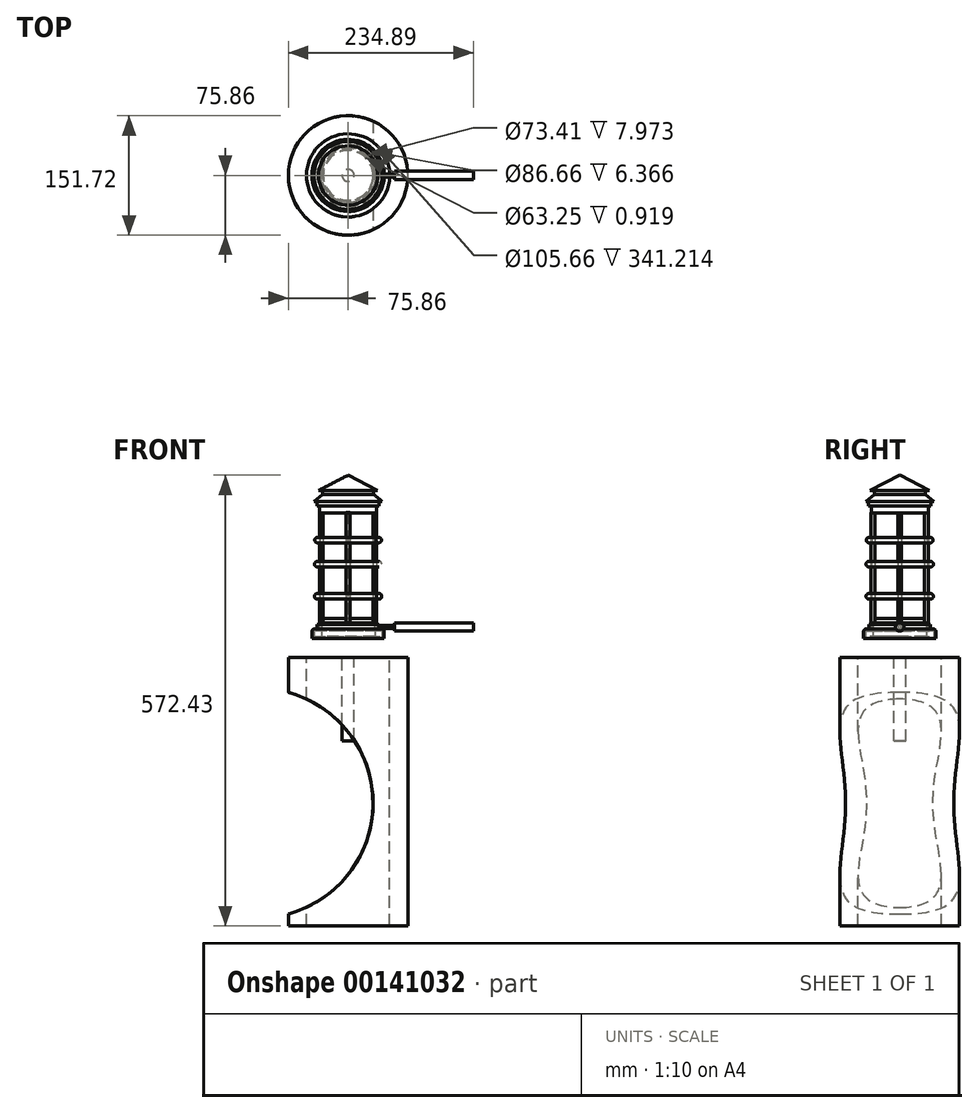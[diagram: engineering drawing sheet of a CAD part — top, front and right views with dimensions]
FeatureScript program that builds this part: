
annotation { "Feature Type Name" : "Feature", "Feature Type Description" : "" }
export const myFeature = defineFeature(function(context is Context, id is Id, definition is map)
    precondition{}
    {
        {
            var Q0;
            Q0=qCreatedBy(makeId("Front.planeOp"),FACE);
            var sketch = newSketch(context, id + "F0", { "sketchPlane" : qUnion([Q0])});
            skLineSegment(sketch, "E0", {"start": v(0, -64.78) * mm, "end": v(-52.83, -64.78) * mm});
            skLineSegment(sketch, "E1", {"start": v(-52.83, -64.78) * mm, "end": v(-45.18, -57.68) * mm});
            skLineSegment(sketch, "E2", {"start": v(-45.18, -57.68) * mm, "end": v(-45.18, -42.8) * mm});
            skLineSegment(sketch, "E3", {"start": v(-45.18, -42.8) * mm, "end": v(-47.57, -42.8) * mm});
            skLineSegment(sketch, "E4", {"start": v(-47.57, -42.8) * mm, "end": v(-47.57, -40.94) * mm});
            skLineSegment(sketch, "E5", {"start": v(-47.57, -40.94) * mm, "end": v(0, -40.94) * mm});
            skLineSegment(sketch, "E6", {"start": v(0, -40.94) * mm, "end": v(0, -64.78) * mm, "construction": true});
            skSolve(sketch);
        }
        {
            var Q0;
            Q0=sQuery(id+"F0.wireOp",EDGE,"E5");
            var Q1;
            Q1=sQuery(id+"F0.wireOp",EDGE,"E4");
            var Q2;
            Q2=sQuery(id+"F0.wireOp",EDGE,"E3");
            var Q3;
            Q3=sQuery(id+"F0.wireOp",EDGE,"E2");
            var Q4;
            Q4=sQuery(id+"F0.wireOp",EDGE,"E1");
            var Q5;
            Q5=sQuery(id+"F0.wireOp",EDGE,"E0");
            var Q6;
            Q6=sQuery(id+"F0.wireOp",EDGE,"E6");
            revolve(context, id + "F1", {"bodyType" : ToolBodyType.SURFACE, "surfaceEntities" : qUnion([Q0, Q1, Q2, Q3, Q4, Q5]), "axis" : qUnion([Q6]), "revolveType" : RevolveType.FULL});
        }
        {
            var Q0;
            Q0=makeQuery(id+"F1.opRevolve","SWEPT_FACE",FACE,{"disambiguationData":[OSD([sQuery(id+"F0.wireOp",EDGE,"E5")])]});
            var sketch = newSketch(context, id + "F2", { "sketchPlane" : qUnion([Q0])});
            skCircle(sketch, "E7", {"center": v(0, 0) * mm, "radius": 45.87 * mm});
            skSolve(sketch);
        }
        {
            var Q0;
            Q0=makeQuery(id+"F2.imprint","IMPRINT",FACE,{"disambiguationData":[TD([[makeQuery(id+"F2.imprint","IMPRINT",EDGE,{"derivedFrom":sQuery(id+"F2.wireOp",EDGE,"E7")}),1.0]])]});
            extrude(context, id + "F3", {"entities" : qUnion([Q0]), "depth" : 12.23 * mm});
        }
        {
            var Q0;
            Q0=makeQuery(id+"F3.opExtrude","CAP_EDGE",EDGE,{"disambiguationData":[OSD([sQuery(id+"F2.wireOp",EDGE,"E7")])],"isStart":false});
            fillet(context, id + "F4", {"entities" : qUnion([Q0]), "radius" : 3.32 * mm, "tangentPropagation" : true, "allowEdgeOverflow" : false});
        }
        {
            var Q0;
            Q0=makeQuery(id+"F3.opExtrude","CAP_FACE",FACE,{"disambiguationData":[OSD([sQuery(id+"F2.wireOp",EDGE,"E7")])],"isStart":false});
            var sketch = newSketch(context, id + "F5", { "sketchPlane" : qUnion([Q0])});
            skCircle(sketch, "E8", {"center": v(0, 0) * mm, "radius": 39.24 * mm});
            skSolve(sketch);
        }
        {
            var Q0;
            Q0=makeQuery(id+"F5.imprint","IMPRINT",FACE,{"disambiguationData":[TD([[makeQuery(id+"F5.imprint","IMPRINT",EDGE,{"derivedFrom":sQuery(id+"F5.wireOp",EDGE,"E8")}),1.0]])]});
            extrude(context, id + "F6", {"entities" : qUnion([Q0]), "operationType" : NewBodyOperationType.ADD, "depth" : 5.43 * mm});
        }
        {
            var Q0;
            Q0=makeQuery(id+"F6.opExtrude","CAP_FACE",FACE,{"disambiguationData":[OSD([sQuery(id+"F5.wireOp",EDGE,"E8")])],"isStart":false});
            shell(context, id + "F7", {"entities" : qUnion([Q0]), "thickness" : 2.54 * mm});
        }
        {
            var Q0;
            {var subQ0=sQuery(id+"F2.wireOp",EDGE,"E7");Q0=makeQuery(id+"F7.opShell","OFFSET_FACE",FACE,{"disambiguationData":[OSD([subQ0]),TDD([makeQuery(id+"F3.opExtrude","CAP_FACE",FACE,{"disambiguationData":[OSD([subQ0])],"isStart":true})])]});}
            var sketch = newSketch(context, id + "F8", { "sketchPlane" : qUnion([Q0])});
            skCircle(sketch, "E9", {"center": v(0, 0) * mm, "radius": 33.95 * mm});
            skSolve(sketch);
        }
        {
            var Q0;
            Q0=qSketchRegion(id+"F8",true);
            extrude(context, id + "F9", {"entities" : qUnion([Q0]), "operationType" : NewBodyOperationType.ADD, "depth" : 17.16 * mm});
        }
        {
            var Q0;
            Q0=makeQuery(id+"F9.opExtrude","CAP_FACE",FACE,{"disambiguationData":[OSD([sQuery(id+"F8.wireOp",EDGE,"E9")])],"isStart":false});
            var sketch = newSketch(context, id + "F10", { "sketchPlane" : qUnion([Q0])});
            skCircle(sketch, "E10", {"center": v(0, 0) * mm, "radius": 31.65 * mm});
            skSolve(sketch);
        }
        {
            var Q0;
            Q0=qSketchRegion(id+"F10",true);
            extrude(context, id + "F11", {"entities" : qUnion([Q0]), "operationType" : NewBodyOperationType.ADD, "depth" : 5.86 * mm});
        }
        {
            var Q0;
            Q0=makeQuery(id+"F9.opExtrude","CAP_FACE",FACE,{"disambiguationData":[OSD([sQuery(id+"F8.wireOp",EDGE,"E9")])],"isStart":false});
            var sketch = newSketch(context, id + "F12", { "sketchPlane" : qUnion([Q0])});
            skCircle(sketch, "E11", {"center": v(33.95, 0) * mm, "radius": 2.3 * mm});
            skCircle(sketch, "E12", {"center": v(-33.95, 0) * mm, "radius": 2.3 * mm});
            skCircle(sketch, "E13", {"center": v(0, 33.95) * mm, "radius": 2.3 * mm});
            skCircle(sketch, "E14", {"center": v(0, -33.95) * mm, "radius": 2.34 * mm});
            skSolve(sketch);
        }
        {
            var Q0;
            {var subQ0=sQuery(id+"F12.wireOp",EDGE,"E11");var subQ1=makeQuery(id+"F9.opExtrude","CAP_EDGE",EDGE,{"disambiguationData":[OSD([sQuery(id+"F8.wireOp",EDGE,"E9")])],"isStart":false});var subQ2=makeQuery(id+"F12.imprint","INTERSECT",VERTEX,{"disambiguationData":[OD(0.0)],"derivedFrom":[subQ1,subQ0]});Q0=makeQuery(id+"F12.imprint","IMPRINT",FACE,{"disambiguationData":[TD([[makeQuery(id+"F12.imprint","IMPRINT",EDGE,{"disambiguationData":[TD([[subQ2,1.0]])],"derivedFrom":subQ0}),1.0]])]});}
            var Q1;
            {var subQ0=sQuery(id+"F12.wireOp",EDGE,"E12");var subQ1=makeQuery(id+"F9.opExtrude","CAP_EDGE",EDGE,{"disambiguationData":[OSD([sQuery(id+"F8.wireOp",EDGE,"E9")])],"isStart":false});var subQ2=makeQuery(id+"F12.imprint","INTERSECT",VERTEX,{"disambiguationData":[OD(0.0)],"derivedFrom":[subQ1,subQ0]});Q1=makeQuery(id+"F12.imprint","IMPRINT",FACE,{"disambiguationData":[TD([[makeQuery(id+"F12.imprint","IMPRINT",EDGE,{"disambiguationData":[TD([[subQ2,1.0]])],"derivedFrom":subQ0}),1.0]])]});}
            var Q2;
            {var subQ0=sQuery(id+"F12.wireOp",EDGE,"E13");var subQ1=makeQuery(id+"F9.opExtrude","CAP_EDGE",EDGE,{"disambiguationData":[OSD([sQuery(id+"F8.wireOp",EDGE,"E9")])],"isStart":false});var subQ2=makeQuery(id+"F12.imprint","INTERSECT",VERTEX,{"disambiguationData":[OD(0.0)],"derivedFrom":[subQ1,subQ0]});Q2=makeQuery(id+"F12.imprint","IMPRINT",FACE,{"disambiguationData":[TD([[makeQuery(id+"F12.imprint","IMPRINT",EDGE,{"disambiguationData":[TD([[subQ2,1.0]])],"derivedFrom":subQ0}),1.0]])]});}
            var Q3;
            {var subQ0=sQuery(id+"F12.wireOp",EDGE,"E13");var subQ1=makeQuery(id+"F9.opExtrude","CAP_EDGE",EDGE,{"disambiguationData":[OSD([sQuery(id+"F8.wireOp",EDGE,"E9")])],"isStart":false});var subQ2=makeQuery(id+"F12.imprint","INTERSECT",VERTEX,{"disambiguationData":[OD(0.0)],"derivedFrom":[subQ1,subQ0]});Q3=makeQuery(id+"F12.imprint","IMPRINT",FACE,{"disambiguationData":[TD([[makeQuery(id+"F12.imprint","IMPRINT",EDGE,{"disambiguationData":[TD([[subQ2,-1.0]])],"derivedFrom":subQ0}),1.0]])]});}
            var Q4;
            {var subQ0=sQuery(id+"F12.wireOp",EDGE,"E12");var subQ1=makeQuery(id+"F9.opExtrude","CAP_EDGE",EDGE,{"disambiguationData":[OSD([sQuery(id+"F8.wireOp",EDGE,"E9")])],"isStart":false});var subQ2=makeQuery(id+"F12.imprint","INTERSECT",VERTEX,{"disambiguationData":[OD(0.0)],"derivedFrom":[subQ1,subQ0]});Q4=makeQuery(id+"F12.imprint","IMPRINT",FACE,{"disambiguationData":[TD([[makeQuery(id+"F12.imprint","IMPRINT",EDGE,{"disambiguationData":[TD([[subQ2,-1.0]])],"derivedFrom":subQ0}),1.0]])]});}
            var Q5;
            {var subQ0=sQuery(id+"F12.wireOp",EDGE,"E11");var subQ1=makeQuery(id+"F9.opExtrude","CAP_EDGE",EDGE,{"disambiguationData":[OSD([sQuery(id+"F8.wireOp",EDGE,"E9")])],"isStart":false});var subQ2=makeQuery(id+"F12.imprint","INTERSECT",VERTEX,{"disambiguationData":[OD(0.0)],"derivedFrom":[subQ1,subQ0]});Q5=makeQuery(id+"F12.imprint","IMPRINT",FACE,{"disambiguationData":[TD([[makeQuery(id+"F12.imprint","IMPRINT",EDGE,{"disambiguationData":[TD([[subQ2,-1.0]])],"derivedFrom":subQ0}),1.0]])]});}
            var Q6;
            {var subQ0=sQuery(id+"F12.wireOp",EDGE,"E14");var subQ1=makeQuery(id+"F9.opExtrude","CAP_EDGE",EDGE,{"disambiguationData":[OSD([sQuery(id+"F8.wireOp",EDGE,"E9")])],"isStart":false});var subQ2=makeQuery(id+"F12.imprint","INTERSECT",VERTEX,{"disambiguationData":[OD(0.0)],"derivedFrom":[subQ1,subQ0]});Q6=makeQuery(id+"F12.imprint","IMPRINT",FACE,{"disambiguationData":[TD([[makeQuery(id+"F12.imprint","IMPRINT",EDGE,{"disambiguationData":[TD([[subQ2,-1.0]])],"derivedFrom":subQ0}),1.0]])]});}
            var Q7;
            {var subQ0=sQuery(id+"F12.wireOp",EDGE,"E14");var subQ1=makeQuery(id+"F9.opExtrude","CAP_EDGE",EDGE,{"disambiguationData":[OSD([sQuery(id+"F8.wireOp",EDGE,"E9")])],"isStart":false});var subQ2=makeQuery(id+"F12.imprint","INTERSECT",VERTEX,{"disambiguationData":[OD(0.0)],"derivedFrom":[subQ1,subQ0]});Q7=makeQuery(id+"F12.imprint","IMPRINT",FACE,{"disambiguationData":[TD([[makeQuery(id+"F12.imprint","IMPRINT",EDGE,{"disambiguationData":[TD([[subQ2,1.0]])],"derivedFrom":subQ0}),1.0]])]});}
            extrude(context, id + "F13", {"entities" : qUnion([Q0, Q1, Q2, Q3, Q4, Q5, Q6, Q7]), "depth" : 140.45 * mm});
        }
        {
            var Q0;
            Q0=makeQuery(id+"F11.opExtrude","CAP_FACE",FACE,{"disambiguationData":[OSD([sQuery(id+"F10.wireOp",EDGE,"E10")])],"isStart":false});
            extrude(context, id + "F14", {"entities" : qUnion([Q0]), "depth" : 134.56 * mm});
        }
        {
            var Q0;
            Q0=makeQuery(id+"F14.opExtrude","CAP_FACE",FACE,{"disambiguationData":[OSD([sQuery(id+"F10.wireOp",EDGE,"E10")])],"isStart":false});
            shell(context, id + "F15", {"entities" : qUnion([Q0]), "thickness" : 0.03 * mm});
        }
        {
            var Q0;
            {var subQ0=sQuery(id+"F10.wireOp",EDGE,"E10");Q0=makeQuery(id+"F15.opShell","OFFSET_FACE",FACE,{"disambiguationData":[OSD([subQ0]),TDD([makeQuery(id+"F14.opExtrude","CAP_FACE",FACE,{"disambiguationData":[OSD([subQ0])],"isStart":true})])]});}
            extrude(context, id + "F16", {"entities" : qUnion([Q0]), "operationType" : NewBodyOperationType.ADD, "depth" : 133.61 * mm});
        }
        {
            var Q0;
            Q0=makeQuery(id+"F16.opExtrude","CAP_FACE",FACE,{"disambiguationData":[OSD([sQuery(id+"F10.wireOp",EDGE,"E10")])],"isStart":false});
            var sketch = newSketch(context, id + "F17", { "sketchPlane" : qUnion([Q0])});
            skCircle(sketch, "E15", {"center": v(0, 0) * mm, "radius": 36.18 * mm});
            skSolve(sketch);
        }
        {
            var Q0;
            Q0=qSketchRegion(id+"F17",true);
            extrude(context, id + "F18", {"entities" : qUnion([Q0]), "depth" : 8.96 * mm});
        }
        {
            var Q0;
            Q0=makeQuery(id+"F18.opExtrude","CAP_FACE",FACE,{"disambiguationData":[OSD([sQuery(id+"F17.wireOp",EDGE,"E15")])],"isStart":false});
            var sketch = newSketch(context, id + "F19", { "sketchPlane" : qUnion([Q0])});
            skCircle(sketch, "E16", {"center": v(0, 0) * mm, "radius": 39.6 * mm});
            skSolve(sketch);
        }
        {
            var Q0;
            Q0=makeQuery(id+"F19.imprint","IMPRINT",FACE,{"disambiguationData":[TD([[makeQuery(id+"F19.imprint","IMPRINT",EDGE,{"derivedFrom":sQuery(id+"F19.wireOp",EDGE,"E16")}),1.0]])]});
            var Q1;
            Q1=makeQuery(id+"F19.imprint","IMPRINT",FACE,{"disambiguationData":[TD([[makeQuery(id+"F19.imprint","IMPRINT",EDGE,{"derivedFrom":makeQuery(id+"F18.opExtrude","CAP_EDGE",EDGE,{"disambiguationData":[OSD([sQuery(id+"F17.wireOp",EDGE,"E15")])],"isStart":false})}),1.0]])]});
            extrude(context, id + "F20", {"entities" : qUnion([Q0, Q1]), "operationType" : NewBodyOperationType.ADD, "depth" : 6.14 * mm});
        }
        {
            var Q0;
            Q0=makeQuery(id+"F20.opExtrude","CAP_FACE",FACE,{"disambiguationData":[OSD([sQuery(id+"F19.wireOp",EDGE,"E16")])],"isStart":false});
            var sketch = newSketch(context, id + "F21", { "sketchPlane" : qUnion([Q0])});
            skSolve(sketch);
        }
        {
            var Q0;
            Q0=makeQuery(id+"F21.imprint","IMPRINT",FACE,{"disambiguationData":[TD([[makeQuery(id+"F21.imprint","IMPRINT",EDGE,{"derivedFrom":makeQuery(id+"F20.opExtrude","CAP_EDGE",EDGE,{"disambiguationData":[OSD([sQuery(id+"F19.wireOp",EDGE,"E16")])],"isStart":false})}),1.0]])]});
            var sketch = newSketch(context, id + "F22", { "sketchPlane" : qUnion([Q0])});
            skSolve(sketch);
        }
        {
            var Q0;
            Q0=makeQuery(id+"F22.imprint","IMPRINT",FACE,{"disambiguationData":[TD([[makeQuery(id+"F22.imprint","IMPRINT",EDGE,{"derivedFrom":makeQuery(id+"F21.imprint","IMPRINT",EDGE,{"derivedFrom":makeQuery(id+"F20.opExtrude","CAP_EDGE",EDGE,{"disambiguationData":[OSD([sQuery(id+"F19.wireOp",EDGE,"E16")])],"isStart":false})})}),1.0]])]});
            var sketch = newSketch(context, id + "F23", { "sketchPlane" : qUnion([Q0])});
            skCircle(sketch, "E17", {"center": v(0, 0) * mm, "radius": 5.35 * mm});
            skSolve(sketch);
        }
        {
            var Q0;
            Q0=makeQuery(id+"F23.imprint","IMPRINT",FACE,{"disambiguationData":[TD([[makeQuery(id+"F23.imprint","IMPRINT",EDGE,{"derivedFrom":sQuery(id+"F23.wireOp",EDGE,"E17")}),1.0]])]});
            extrude(context, id + "F24", {"entities" : qUnion([Q0]), "operationType" : NewBodyOperationType.ADD, "depth" : 28.78 * mm});
        }
        {
            var Q0;
            Q0=qCreatedBy(makeId("Front.planeOp"),FACE);
            var sketch = newSketch(context, id + "F25", { "sketchPlane" : qUnion([Q0])});
            skLineSegment(sketch, "E18", {"start": v(0, 148) * mm, "end": v(0, 133.15) * mm});
            skLineSegment(sketch, "E19", {"start": v(0, 133.15) * mm, "end": v(43.2, 133.15) * mm});
            skLineSegment(sketch, "E20", {"start": v(43.2, 133.15) * mm, "end": v(32.35, 142.24) * mm});
            skLineSegment(sketch, "E21", {"start": v(32.35, 142.24) * mm, "end": v(32.35, 147.08) * mm});
            skLineSegment(sketch, "E22", {"start": v(32.35, 147.08) * mm, "end": v(37.62, 147.08) * mm});
            skLineSegment(sketch, "E23", {"start": v(37.62, 147.08) * mm, "end": v(0, 166.44) * mm});
            skLineSegment(sketch, "E24", {"start": v(0, 166.44) * mm, "end": v(0, 148) * mm});
            skSolve(sketch);
        }
        {
            var Q0;
            Q0=makeQuery(id+"F25.imprint","IMPRINT",FACE,{"disambiguationData":[TD([[makeQuery(id+"F25.imprint","IMPRINT",EDGE,{"derivedFrom":sQuery(id+"F25.wireOp",EDGE,"E18")}),1.0]])]});
            var Q1;
            Q1=sQuery(id+"F25.wireOp",EDGE,"E24");
            revolve(context, id + "F26", {"operationType" : NewBodyOperationType.ADD, "entities" : qUnion([Q0]), "axis" : qUnion([Q1]), "revolveType" : RevolveType.FULL});
        }
        {
            var Q0;
            Q0=qCreatedBy(makeId("Right.planeOp"),FACE);
            var sketch = newSketch(context, id + "F27", { "sketchPlane" : qUnion([Q0])});
            skCircle(sketch, "E25", {"center": v(-39.38, 53.45) * mm, "radius": 3.44 * mm});
            skCircle(sketch, "E26", {"center": v(-39.3, 12.6) * mm, "radius": 3.5 * mm});
            skCircle(sketch, "E27", {"center": v(-38.89, 84.08) * mm, "radius": 3.5 * mm});
            skSolve(sketch);
        }
        {
            var Q0;
            Q0=sQuery(id+"F27.wireOp",EDGE,"E25");
            var Q1;
            Q1=makeQuery(id+"F14.opExtrude","SWEPT_FACE",FACE,{"disambiguationData":[OSD([sQuery(id+"F10.wireOp",EDGE,"E10")])]});
            revolve(context, id + "F28", {"bodyType" : ToolBodyType.SURFACE, "surfaceEntities" : qUnion([Q0]), "axis" : qUnion([Q1]), "revolveType" : RevolveType.FULL});
        }
        {
            var Q0;
            Q0=qSketchRegion(id+"F27",true);
            var Q1;
            Q1=makeQuery(id+"F14.opExtrude","SWEPT_FACE",FACE,{"disambiguationData":[OSD([sQuery(id+"F10.wireOp",EDGE,"E10")])]});
            revolve(context, id + "F29", {"entities" : qUnion([Q0]), "axis" : qUnion([Q1]), "revolveType" : RevolveType.FULL});
        }
        {
            var Q0;
            Q0=qSketchRegion(id+"F27",true);
            var Q1;
            Q1=makeQuery(id+"F14.opExtrude","SWEPT_FACE",FACE,{"disambiguationData":[OSD([sQuery(id+"F10.wireOp",EDGE,"E10")])]});
            revolve(context, id + "F30", {"entities" : qUnion([Q0]), "axis" : qUnion([Q1]), "revolveType" : RevolveType.FULL});
        }
        {
            var Q0;
            Q0=qCreatedBy(makeId("Right.planeOp"),FACE);
            var sketch = newSketch(context, id + "F31", { "sketchPlane" : qUnion([Q0])});
            skCircle(sketch, "E28", {"center": v(0, -26.4) * mm, "radius": 1.99 * mm});
            skSolve(sketch);
        }
        {
            var Q0;
            Q0=qSketchRegion(id+"F31",true);
            extrude(context, id + "F32", {"entities" : qUnion([Q0]), "operationType" : NewBodyOperationType.ADD, "depth" : 64.6 * mm});
        }
        {
            var Q0;
            Q0=makeQuery(id+"F32.opExtrude","CAP_FACE",FACE,{"disambiguationData":[OSD([sQuery(id+"F31.wireOp",EDGE,"E28")])],"isStart":false});
            var sketch = newSketch(context, id + "F33", { "sketchPlane" : qUnion([Q0])});
            skCircle(sketch, "E29", {"center": v(0, -26.4) * mm, "radius": 5.31 * mm});
            skSolve(sketch);
        }
        {
            var Q0;
            Q0=makeQuery(id+"F33.imprint","IMPRINT",FACE,{"disambiguationData":[TD([[makeQuery(id+"F33.imprint","IMPRINT",EDGE,{"derivedFrom":sQuery(id+"F33.wireOp",EDGE,"E29")}),1.0]])]});
            var Q1;
            Q1=makeQuery(id+"F33.imprint","IMPRINT",FACE,{"disambiguationData":[TD([[makeQuery(id+"F33.imprint","IMPRINT",EDGE,{"derivedFrom":makeQuery(id+"F32.opExtrude","CAP_EDGE",EDGE,{"disambiguationData":[OSD([sQuery(id+"F31.wireOp",EDGE,"E28")])],"isStart":false})}),1.0]])]});
            extrude(context, id + "F34", {"entities" : qUnion([Q0, Q1]), "operationType" : NewBodyOperationType.ADD, "oppositeDirection" : true, "depth" : 5.38 * mm});
        }
        {
            var Q0;
            Q0=makeQuery(id+"F1.opRevolve","SWEPT_FACE",FACE,{"disambiguationData":[OSD([sQuery(id+"F0.wireOp",EDGE,"E0")])]});
            var sketch = newSketch(context, id + "F35", { "sketchPlane" : qUnion([Q0])});
            skCircle(sketch, "E30", {"center": v(0, 0) * mm, "radius": 75.86 * mm});
            skSolve(sketch);
        }
        {
            var Q0;
            Q0=makeQuery(id+"F35.imprint","IMPRINT",FACE,{"disambiguationData":[TD([[makeQuery(id+"F35.imprint","IMPRINT",EDGE,{"derivedFrom":sQuery(id+"F35.wireOp",EDGE,"E30")}),1.0]])]});
            extrude(context, id + "F36", {"entities" : qUnion([Q0]), "depth" : 341.2 * mm});
        }
        {
            var Q0;
            Q0=qCreatedBy(makeId("Front.planeOp"),FACE);
            var sketch = newSketch(context, id + "F37", { "sketchPlane" : qUnion([Q0])});
            skCircle(sketch, "E31", {"center": v(-114.13, -250.23) * mm, "radius": 145.9 * mm});
            skSolve(sketch);
        }
        {
            var Q0;
            Q0=makeQuery(id+"F37.imprint","IMPRINT",FACE,{"disambiguationData":[TD([[makeQuery(id+"F37.imprint","IMPRINT",EDGE,{"derivedFrom":sQuery(id+"F37.wireOp",EDGE,"E31")}),1.0]])]});
            extrude(context, id + "F38", {"entities" : qUnion([Q0]), "operationType" : NewBodyOperationType.REMOVE, "endBound" : BoundingType.SYMMETRIC, "oppositeDirection" : true, "depth" : 435.72 * mm});
        }
        {
            var Q0;
            Q0=qCreatedBy(makeId("Top.planeOp"),FACE);
            var sketch = newSketch(context, id + "F39", { "sketchPlane" : qUnion([Q0])});
            skCircle(sketch, "E32", {"center": v(0, 0) * mm, "radius": 22.5 * mm});
            skSolve(sketch);
        }
        {
            var Q0;
            Q0 = qSketchRegion(id + "F39", true);
            var Q1;
            Q1=sQuery(id+"F39.wireOp",EDGE,"E32");
            extrude(context, id + "F40", {"entities" : qUnion([Q0]), "bodyType" : ToolBodyType.SURFACE, "operationType" : NewBodyOperationType.REMOVE, "surfaceEntities" : qUnion([Q1]), "depth" : 249.58 * mm});
        }
        {
            var Q0;
            Q0=makeQuery(id+"F34.boolean.opBoolean","MERGE",FACE,{"derivedFrom":[makeQuery(id+"F32.opExtrude","CAP_FACE",FACE,{"disambiguationData":[OSD([sQuery(id+"F31.wireOp",EDGE,"E28")])],"isStart":false}),makeQuery(id+"F34.opExtrude","CAP_FACE",FACE,{"disambiguationData":[OSD([sQuery(id+"F33.wireOp",EDGE,"E29")])],"isStart":true})]});
            extrude(context, id + "F41", {"entities" : qUnion([Q0]), "operationType" : NewBodyOperationType.ADD, "depth" : 94.43 * mm});
        }
        {
            var Q0;
            Q0=makeQuery(id+"F1.opRevolve","SWEPT_FACE",FACE,{"disambiguationData":[OSD([sQuery(id+"F0.wireOp",EDGE,"E0")])]});
            var sketch = newSketch(context, id + "F42", { "sketchPlane" : qUnion([Q0])});
            skCircle(sketch, "E33", {"center": v(0, 0) * mm, "radius": 7.66 * mm});
            skSolve(sketch);
        }
        {
            var Q0;
            Q0 = qSketchRegion(id + "F42", true);
            extrude(context, id + "F43", {"entities" : qUnion([Q0]), "depth" : 106.48 * mm});
        }
    });
